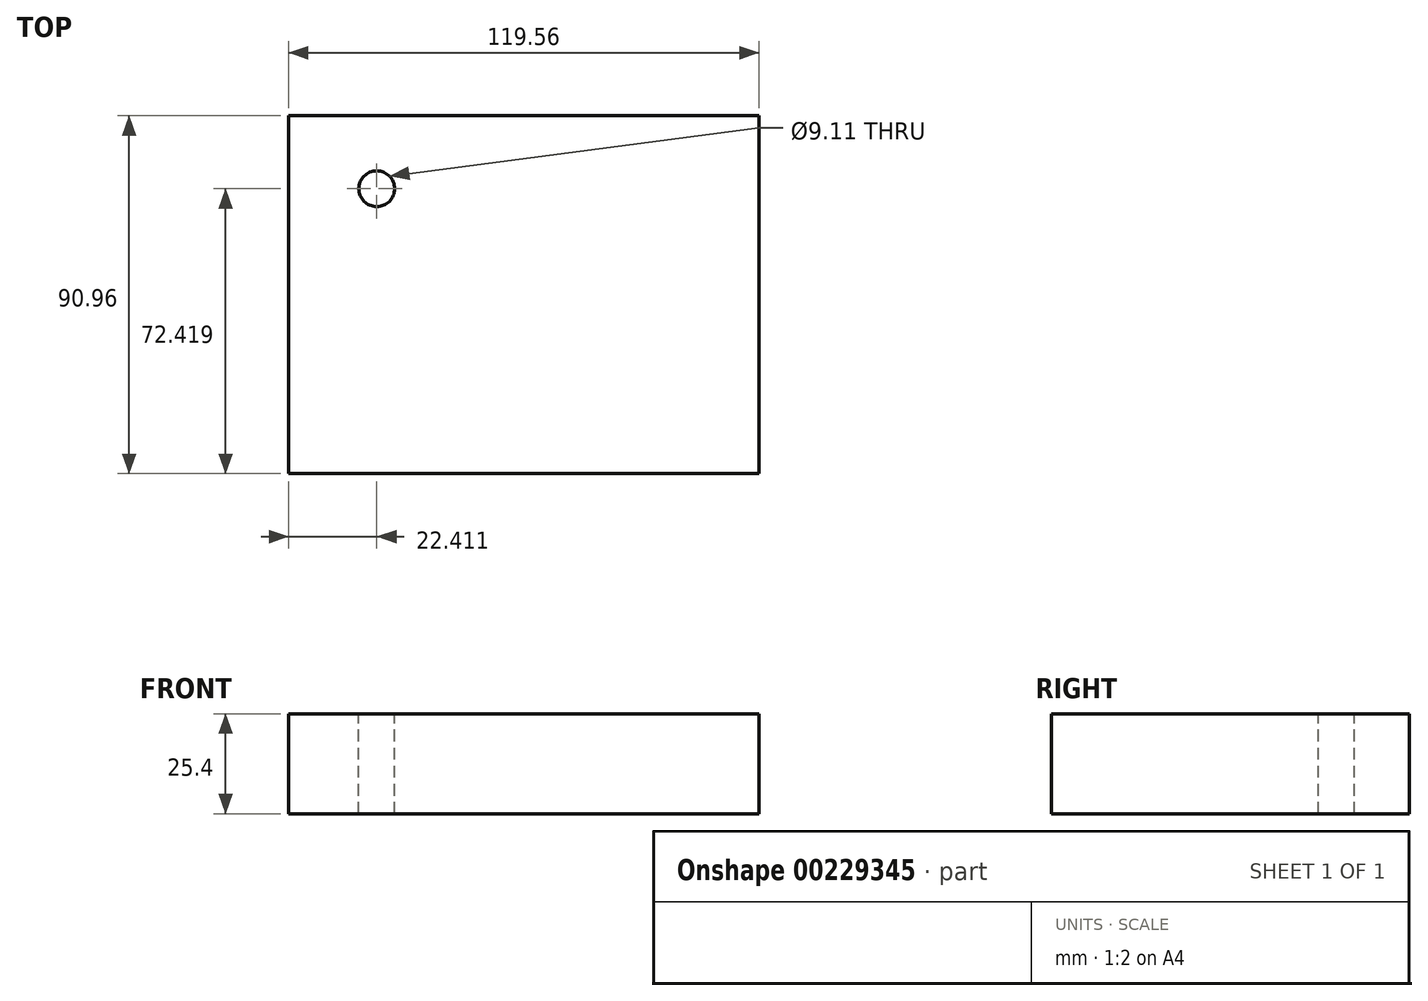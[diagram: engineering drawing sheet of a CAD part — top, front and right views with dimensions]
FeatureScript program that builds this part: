
annotation { "Feature Type Name" : "Feature", "Feature Type Description" : "" }
export const myFeature = defineFeature(function(context is Context, id is Id, definition is map)
    precondition{}
    {
        {
            var Q0;
            Q0=qCreatedBy(makeId("Top.planeOp"),FACE);
            var sketch = newSketch(context, id + "F0", { "sketchPlane" : qUnion([Q0])});
            skLineSegment(sketch, "E0.bottom", {"start": v(59.78, -45.48) * mm, "end": v(-59.78, -45.48) * mm});
            skLineSegment(sketch, "E0.top", {"start": v(59.78, 45.48) * mm, "end": v(-59.78, 45.48) * mm});
            skLineSegment(sketch, "E0.left", {"start": v(59.78, -45.48) * mm, "end": v(59.78, 45.48) * mm});
            skLineSegment(sketch, "E0.right", {"start": v(-59.78, -45.48) * mm, "end": v(-59.78, 45.48) * mm});
            skSolve(sketch);
        }
        {
            var Q0;
            Q0=makeQuery(id+"F0.imprint","IMPRINT",FACE,{"disambiguationData":[TD([[makeQuery(id+"F0.imprint","IMPRINT",EDGE,{"derivedFrom":sQuery(id+"F0.wireOp",EDGE,"E0.bottom")}),-1.0]])]});
            extrude(context, id + "F1", {"entities" : qUnion([Q0]), "depth" : 25.4 * mm});
        }
        {
            var Q0;
            Q0=makeQuery(id+"F1.opExtrude","CAP_FACE",FACE,{"disambiguationData":[OSD([sQuery(id+"F0.wireOp",EDGE,"E0.bottom"),sQuery(id+"F0.wireOp",EDGE,"E0.top"),sQuery(id+"F0.wireOp",EDGE,"E0.left"),sQuery(id+"F0.wireOp",EDGE,"E0.right")])],"isStart":false});
            var sketch = newSketch(context, id + "F2", { "sketchPlane" : qUnion([Q0])});
            skCircle(sketch, "E1", {"center": v(-37.37, 26.94) * mm, "radius": 4.55 * mm});
            skSolve(sketch);
        }
        {
            var Q0;
            Q0=makeQuery(id+"F2.imprint","IMPRINT",FACE,{"disambiguationData":[TD([[makeQuery(id+"F2.imprint","IMPRINT",EDGE,{"derivedFrom":sQuery(id+"F2.wireOp",EDGE,"E1")}),1.0]])]});
            var Q1;
            Q1=sQuery(id+"F2.wireOp",EDGE,"E1");
            extrude(context, id + "F3", {"entities" : qUnion([Q0]), "operationType" : NewBodyOperationType.REMOVE, "surfaceEntities" : qUnion([Q1]), "oppositeDirection" : true, "depth" : 25.4 * mm});
        }
    });
